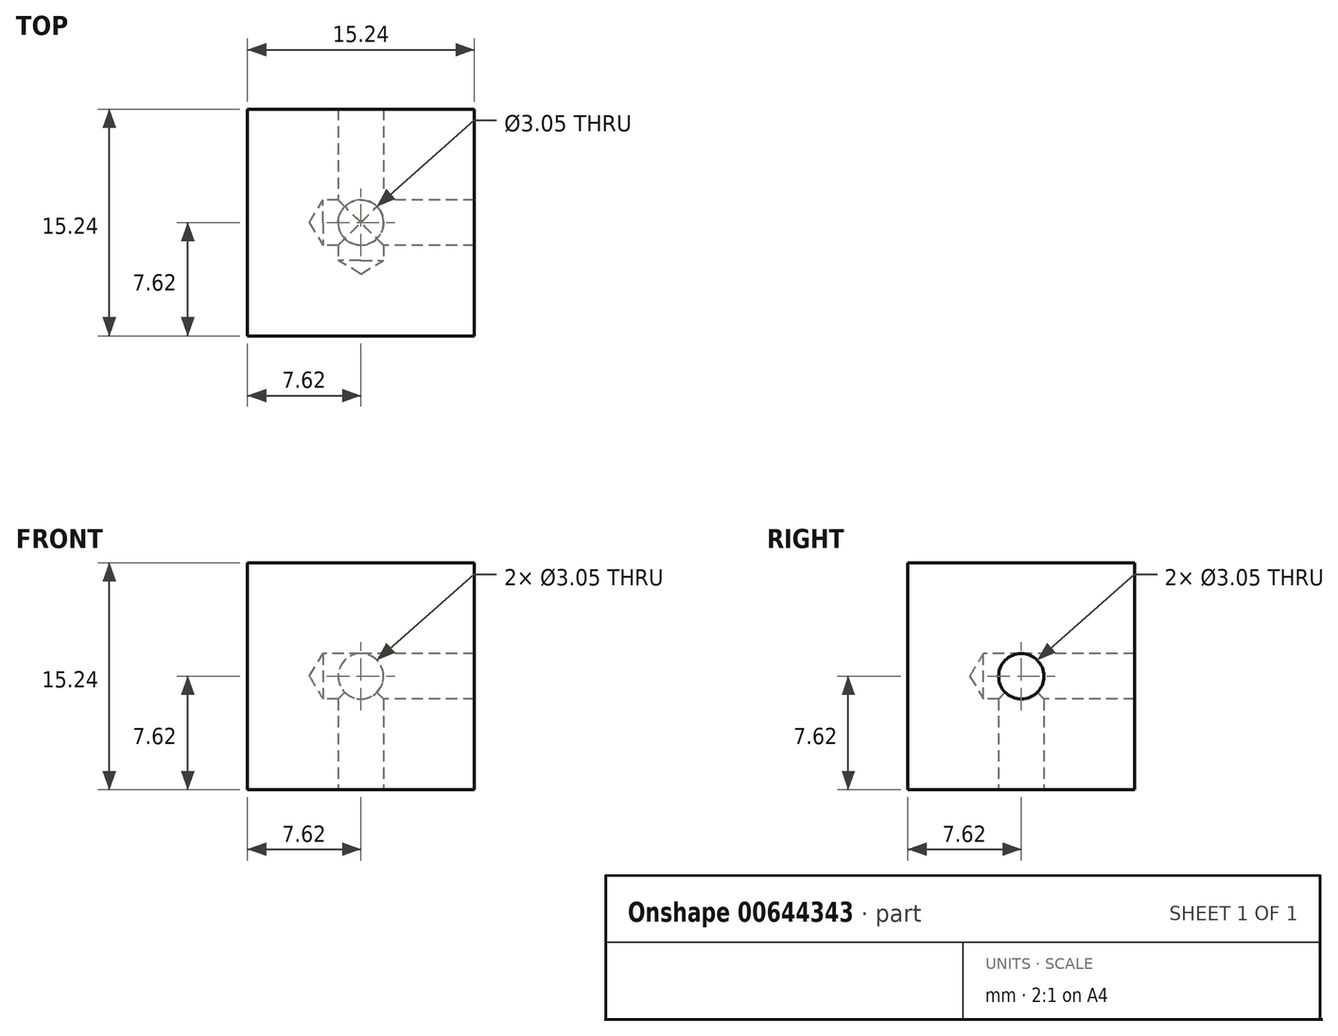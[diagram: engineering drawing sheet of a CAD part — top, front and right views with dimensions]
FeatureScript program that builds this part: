
annotation { "Feature Type Name" : "Feature", "Feature Type Description" : "" }
export const myFeature = defineFeature(function(context is Context, id is Id, definition is map)
    precondition{}
    {
        {
            var Q0;
            Q0=qCreatedBy(makeId("Front.planeOp"),FACE);
            var sketch = newSketch(context, id + "F0", { "sketchPlane" : qUnion([Q0])});
            skLineSegment(sketch, "E0.bottom", {"start": v(7.62, 7.62) * mm, "end": v(-7.62, 7.62) * mm});
            skLineSegment(sketch, "E0.top", {"start": v(7.62, -7.62) * mm, "end": v(-7.62, -7.62) * mm});
            skLineSegment(sketch, "E0.left", {"start": v(7.62, 7.62) * mm, "end": v(7.62, -7.62) * mm});
            skLineSegment(sketch, "E0.right", {"start": v(-7.62, 7.62) * mm, "end": v(-7.62, -7.62) * mm});
            skPoint(sketch, "E0.middle", {"position": v(0, 0) * mm});
            skSolve(sketch);
        }
        {
            var Q0;
            Q0=makeQuery(id+"F0.imprint","IMPRINT",FACE,{"disambiguationData":[TD([[makeQuery(id+"F0.imprint","IMPRINT",EDGE,{"derivedFrom":sQuery(id+"F0.wireOp",EDGE,"E0.bottom")}),1.0]])]});
            extrude(context, id + "F1", {"entities" : qUnion([Q0]), "depth" : 15.24 * mm, "offsetDistance" : 25.4 * mm, "symmetric" : true});
        }
        {
            var Q0;
            Q0=qCreatedBy(makeId("Top.planeOp"),FACE);
            var sketch = newSketch(context, id + "F2", { "sketchPlane" : qUnion([Q0])});
            skPoint(sketch, "E1", {"position": v(0, 0) * mm});
            skSolve(sketch);
        }
        {
            var Q0;
            Q0=sQuery(id+"F2.wireOp",VERTEX,"E1");
            var Q1;
            Q1=makeQuery(id+"F1.opExtrude","SWEPT_BODY",BODY,{"disambiguationData":[OSD([sQuery(id+"F0.wireOp",EDGE,"E0.bottom"),sQuery(id+"F0.wireOp",EDGE,"E0.top"),sQuery(id+"F0.wireOp",EDGE,"E0.left"),sQuery(id+"F0.wireOp",EDGE,"E0.right")])]});
            hole(context, id + "F3", {"style" : HoleStyle.SIMPLE, "endStyle" : HoleEndStyle.BLIND, "holeDiameter" : 3.05 * mm, "majorDiameter" : 6.35 * mm, "holeDepth" : 10.16 * mm, "isTappedThrough" : true, "tappedDepth" : 12.7 * mm, "tapClearance" : 3, "locations" : qUnion([Q0]), "scope" : qUnion([Q1])});
        }
        {
            var Q0;
            Q0=makeQuery(id+"F1.opExtrude","SWEPT_FACE",FACE,{"disambiguationData":[OSD([sQuery(id+"F0.wireOp",EDGE,"E0.left")])]});
            var sketch = newSketch(context, id + "F4", { "sketchPlane" : qUnion([Q0])});
            skCircle(sketch, "E2", {"center": v(0, 0) * mm, "radius": 3.14 * mm});
            skSolve(sketch);
        }
        {
            var Q0;
            Q0=sQuery(id+"F4.wireOp",VERTEX,"E2.center");
            var Q1;
            Q1=makeQuery(id+"F1.opExtrude","SWEPT_BODY",BODY,{"disambiguationData":[OSD([sQuery(id+"F0.wireOp",EDGE,"E0.bottom"),sQuery(id+"F0.wireOp",EDGE,"E0.top"),sQuery(id+"F0.wireOp",EDGE,"E0.left"),sQuery(id+"F0.wireOp",EDGE,"E0.right")])]});
            hole(context, id + "F5", {"style" : HoleStyle.SIMPLE, "endStyle" : HoleEndStyle.BLIND, "holeDiameter" : 3.05 * mm, "majorDiameter" : 6.35 * mm, "holeDepth" : 10.16 * mm, "isTappedThrough" : true, "tappedDepth" : 12.7 * mm, "tapClearance" : 3, "locations" : qUnion([Q0]), "scope" : qUnion([Q1])});
        }
        {
            var Q0;
            Q0=makeQuery(id+"F1.opExtrude","CAP_FACE",FACE,{"disambiguationData":[OSD([sQuery(id+"F0.wireOp",EDGE,"E0.bottom"),sQuery(id+"F0.wireOp",EDGE,"E0.top"),sQuery(id+"F0.wireOp",EDGE,"E0.left"),sQuery(id+"F0.wireOp",EDGE,"E0.right")])],"isStart":true});
            var sketch = newSketch(context, id + "F6", { "sketchPlane" : qUnion([Q0])});
            skCircle(sketch, "E3", {"center": v(0, 0) * mm, "radius": 3.49 * mm});
            skSolve(sketch);
        }
        {
            var Q0;
            Q0=sQuery(id+"F6.wireOp",VERTEX,"E3.center");
            var Q1;
            Q1=makeQuery(id+"F1.opExtrude","SWEPT_BODY",BODY,{"disambiguationData":[OSD([sQuery(id+"F0.wireOp",EDGE,"E0.bottom"),sQuery(id+"F0.wireOp",EDGE,"E0.top"),sQuery(id+"F0.wireOp",EDGE,"E0.left"),sQuery(id+"F0.wireOp",EDGE,"E0.right")])]});
            hole(context, id + "F7", {"style" : HoleStyle.SIMPLE, "endStyle" : HoleEndStyle.BLIND, "holeDiameter" : 3.05 * mm, "majorDiameter" : 6.35 * mm, "holeDepth" : 10.16 * mm, "isTappedThrough" : true, "tappedDepth" : 12.7 * mm, "tapClearance" : 3, "locations" : qUnion([Q0]), "scope" : qUnion([Q1])});
        }
    });
